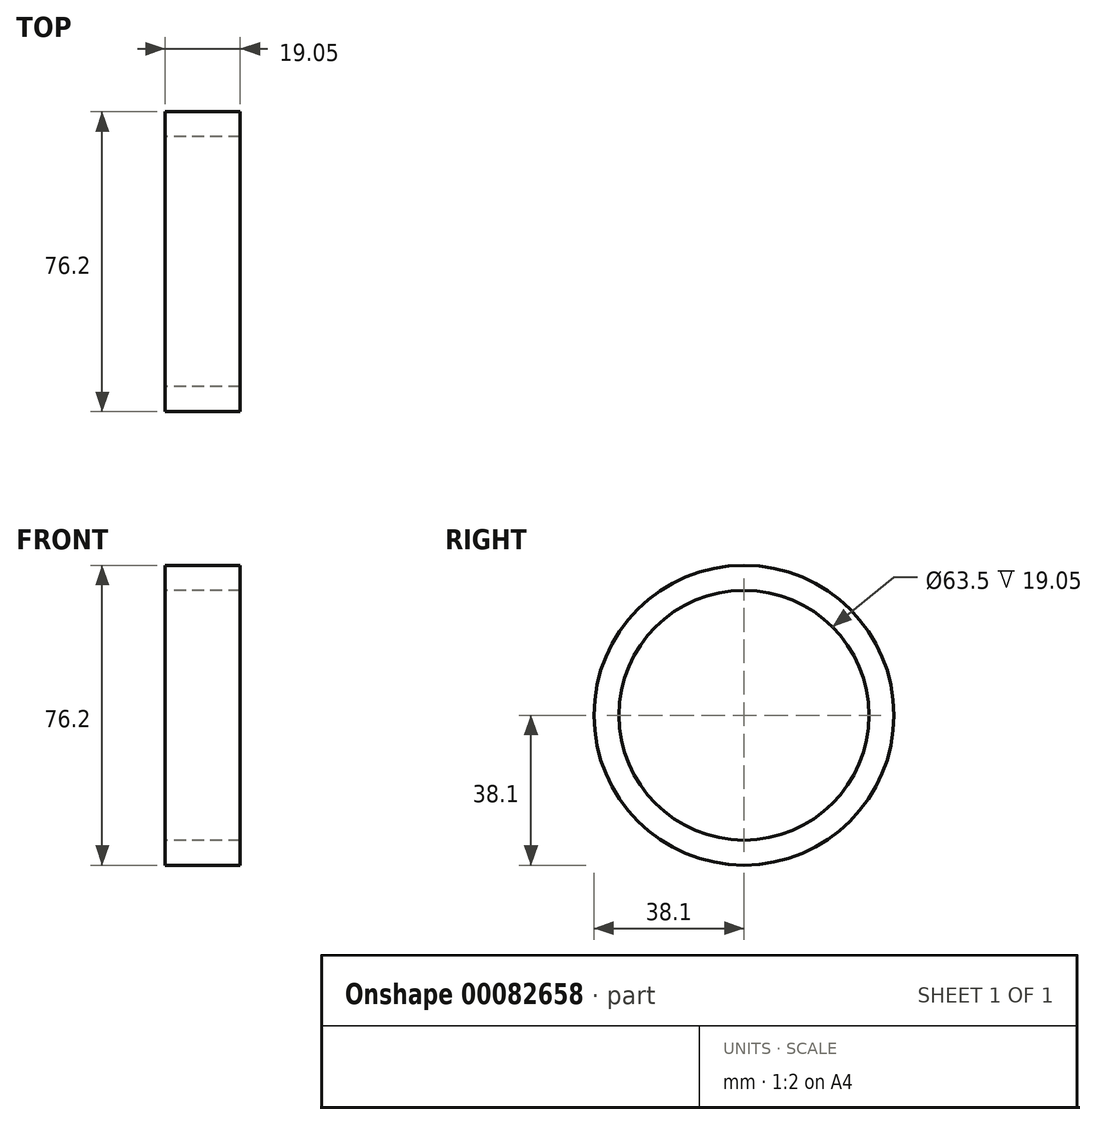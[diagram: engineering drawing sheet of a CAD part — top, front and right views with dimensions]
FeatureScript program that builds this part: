
annotation { "Feature Type Name" : "Feature", "Feature Type Description" : "" }
export const myFeature = defineFeature(function(context is Context, id is Id, definition is map)
    precondition{}
    {
        {
            var Q0;
            Q0=qCreatedBy(makeId("Right.planeOp"),FACE);
            var sketch = newSketch(context, id + "F0", { "sketchPlane" : qUnion([Q0])});
            skCircle(sketch, "E0", {"center": v(0, 0) * mm, "radius": 38.1 * mm});
            skCircle(sketch, "E1", {"center": v(0, 0) * mm, "radius": 31.75 * mm});
            skSolve(sketch);
        }
        {
            var Q0;
            Q0 = qSketchRegion(id + "F0", true);
            extrude(context, id + "F1", {"entities" : qUnion([Q0]), "depth" : 19.05 * mm});
        }
    });
